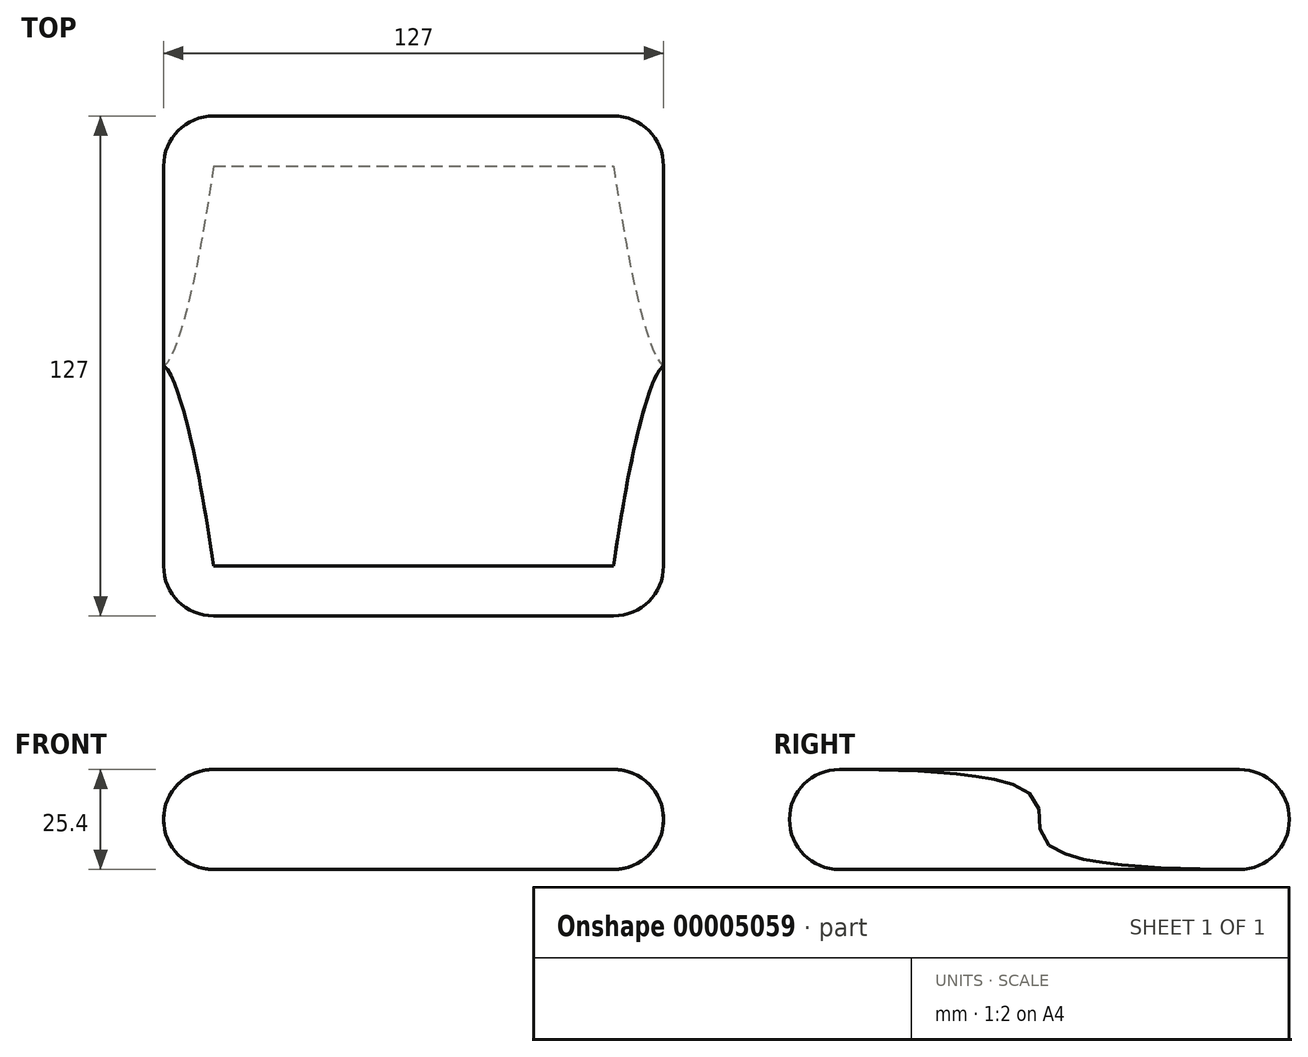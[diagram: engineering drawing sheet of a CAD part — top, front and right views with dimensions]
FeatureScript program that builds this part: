
annotation { "Feature Type Name" : "Feature", "Feature Type Description" : "" }
export const myFeature = defineFeature(function(context is Context, id is Id, definition is map)
    precondition{}
    {
        {
            var Q0;
            Q0=qCreatedBy(makeId("Top.planeOp"),FACE);
            var sketch = newSketch(context, id + "F0", { "sketchPlane" : qUnion([Q0])});
            skLineSegment(sketch, "E0.rect.bottom", {"start": v(-63.5, 63.5) * mm, "end": v(63.5, 63.5) * mm});
            skLineSegment(sketch, "E0.rect.top", {"start": v(-63.5, -63.5) * mm, "end": v(63.5, -63.5) * mm});
            skLineSegment(sketch, "E0.rect.left", {"start": v(-63.5, 63.5) * mm, "end": v(-63.5, -63.5) * mm});
            skLineSegment(sketch, "E0.rect.right", {"start": v(63.5, 63.5) * mm, "end": v(63.5, -63.5) * mm});
            skPoint(sketch, "E0.rect.middle", {"position": v(0, 0) * mm});
            skSolve(sketch);
        }
        {
            var Q0;
            Q0=makeQuery(id+"F0.imprint","IMPRINT",FACE,{"disambiguationData":[TD([[makeQuery(id+"F0.imprint","IMPRINT",EDGE,{"derivedFrom":sQuery(id+"F0.wireOp",EDGE,"E0.rect.bottom")}),-1.0]])]});
            extrude(context, id + "F1", {"entities" : qUnion([Q0]), "depth" : 25.4 * mm});
        }
        {
            var Q0;
            Q0=makeQuery(id+"F1.opExtrude","SWEPT_FACE",FACE,{"disambiguationData":[OSD([sQuery(id+"F0.wireOp",EDGE,"E0.rect.right")])]});
            var sketch = newSketch(context, id + "F2", { "sketchPlane" : qUnion([Q0])});
            skFitSpline(sketch, "E1", {"points": [v(-50.8, 25.4) * mm, v(0, 12.7) * mm, v(50.8, 0) * mm], "startDerivative": vector(304.8, 0) * mm, "endDerivative": vector(304.8, 0) * mm});
            skPoint(sketch, "E2", {"position": v(-63.5, 12.7) * mm});
            skSolve(sketch);
        }
        {
            var Q0;
            Q0=qSketchRegion(id+"F2",true);
            var Q1;
            {var subQ2=sQuery(id+"F2.wireOp",EDGE,"E1");Q1=makeQuery(id+"F2.imprint","IMPRINT",FACE,{"disambiguationData":[TD([[makeQuery(id+"F2.imprint","IMPRINT",EDGE,{"derivedFrom":subQ2}),1.0]])]});}
            extrude(context, id + "F3", {"entities" : qUnion([Q0, Q1]), "operationType" : NewBodyOperationType.REMOVE, "endBound" : BoundingType.THROUGH_ALL, "oppositeDirection" : true, "depth" : 25.4 * mm});
        }
        {
            var Q0;
            Q0=makeQuery(id+"F1.opExtrude","SWEPT_FACE",FACE,{"disambiguationData":[OSD([sQuery(id+"F0.wireOp",EDGE,"E0.rect.right")])]});
            var sketch = newSketch(context, id + "F4", { "sketchPlane" : qUnion([Q0])});
            skLineSegment(sketch, "E3", {"start": v(-50.8, 25.4) * mm, "end": v(63.5, 25.4) * mm});
            skLineSegment(sketch, "E4", {"start": v(63.5, 25.4) * mm, "end": v(63.5, 0) * mm});
            skLineSegment(sketch, "E5", {"start": v(63.5, 0) * mm, "end": v(50.8, 0) * mm});
            skFitSpline(sketch, "E6", {"points": [v(-50.8, 25.4) * mm, v(0, 12.7) * mm, v(50.8, 0) * mm], "startDerivative": vector(304.8, 0) * mm, "endDerivative": vector(304.8, 0) * mm});
            skPoint(sketch, "E7", {"position": v(63.5, 12.7) * mm});
            skSolve(sketch);
        }
        {
            var Q0;
            Q0=makeQuery(id+"F4.imprint","IMPRINT",FACE,{"disambiguationData":[TD([[makeQuery(id+"F4.imprint","IMPRINT",EDGE,{"derivedFrom":sQuery(id+"F4.wireOp",EDGE,"E3")}),-1.0]])]});
            var Q1;
            Q1=makeQuery(id+"F1.opExtrude","SWEPT_FACE",FACE,{"disambiguationData":[OSD([sQuery(id+"F0.wireOp",EDGE,"E0.rect.left")])]});
            extrude(context, id + "F5", {"entities" : qUnion([Q0]), "endBound" : BoundingType.UP_TO_SURFACE, "oppositeDirection" : true, "endBoundEntityFace" : qUnion([Q1]), "depth" : 25.4 * mm});
        }
        {
            var Q0;
            Q0=makeQuery(id+"F1.opExtrude","SWEPT_FACE",FACE,{"disambiguationData":[OSD([sQuery(id+"F0.wireOp",EDGE,"E0.rect.top")])]});
            var sketch = newSketch(context, id + "F6", { "sketchPlane" : qUnion([Q0])});
            skLineSegment(sketch, "E8.bottom", {"start": v(-50.8, 25.4) * mm, "end": v(50.8, 25.4) * mm});
            skLineSegment(sketch, "E8.top", {"start": v(-50.8, 0) * mm, "end": v(50.8, 0) * mm});
            skLineSegment(sketch, "E8.left", {"start": v(-63.5, 12.7) * mm, "end": v(-63.5, 12.7) * mm});
            skLineSegment(sketch, "E8.right", {"start": v(63.5, 12.7) * mm, "end": v(63.5, 12.7) * mm});
            skPoint(sketch, "E9.visualSharp", {"position": v(-63.5, 25.4) * mm});
            skArc(sketch, "E9.filletArc", {"start": v(-50.8, 25.4) * mm, "mid": v(-59.78, 21.68) * mm, "end": v(-63.5, 12.7) * mm});
            skPoint(sketch, "E10.visualSharp", {"position": v(63.5, 25.4) * mm});
            skArc(sketch, "E10.filletArc", {"start": v(63.5, 12.7) * mm, "mid": v(59.78, 21.68) * mm, "end": v(50.8, 25.4) * mm});
            skPoint(sketch, "E11.visualSharp", {"position": v(63.5, 0) * mm});
            skArc(sketch, "E11.filletArc", {"start": v(50.8, 0) * mm, "mid": v(59.78, 3.72) * mm, "end": v(63.5, 12.7) * mm});
            skPoint(sketch, "E12.visualSharp", {"position": v(-63.5, 0) * mm});
            skArc(sketch, "E12.filletArc", {"start": v(-63.5, 12.7) * mm, "mid": v(-59.78, 3.72) * mm, "end": v(-50.8, 0) * mm});
            skLineSegment(sketch, "E13.bottom", {"start": v(-65.32, 27.33) * mm, "end": v(65.32, 27.33) * mm});
            skLineSegment(sketch, "E13.top", {"start": v(-65.32, -1.52) * mm, "end": v(65.32, -1.52) * mm});
            skLineSegment(sketch, "E13.left", {"start": v(-65.32, 27.33) * mm, "end": v(-65.32, -1.52) * mm});
            skLineSegment(sketch, "E13.right", {"start": v(65.32, 27.33) * mm, "end": v(65.32, -1.52) * mm});
            skSolve(sketch);
        }
        {
            var Q0;
            Q0 = qSketchRegion(id + "F6", true);
            extrude(context, id + "F7", {"entities" : qUnion([Q0]), "operationType" : NewBodyOperationType.REMOVE, "endBound" : BoundingType.THROUGH_ALL, "oppositeDirection" : true, "depth" : 25 * mm});
        }
        {
            var Q0;
            Q0=makeQuery(id+"F1.opExtrude","SWEPT_FACE",FACE,{"disambiguationData":[OSD([sQuery(id+"F0.wireOp",EDGE,"E0.rect.top")])]});
            var Q1;
            Q1=makeQuery(id+"F5.opExtrude","SWEPT_FACE",FACE,{"disambiguationData":[OSD([sQuery(id+"F4.wireOp",EDGE,"E4")])]});
            fillet(context, id + "F8", {"entities" : qUnion([Q0, Q1]), "radius" : 12.7 * mm, "tangentPropagation" : true, "allowEdgeOverflow" : false});
        }
    });
